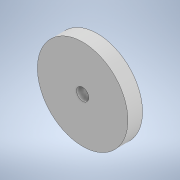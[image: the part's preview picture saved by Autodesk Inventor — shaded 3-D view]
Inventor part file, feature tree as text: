
AUTODESK INVENTOR PART (.ipt)
format: ipt  version: 2021 (Build 250183000, 183)  size: 98,816 bytes
history: native  units: mm
features: extrude x2, sketch x2
ambient origin geometry x8: Origin, YZ Plane, XZ Plane, XY Plane, X Axis, Y Axis, Z Axis, Center Point
bodies: Solid1 (feature_tree)
feature tree (4):
  extrude  "Extrusion1"  Depth=6.0mm TaperAngle=0.0deg
  extrude  "Extrusion2"  Depth=6.0mm TaperAngle=0.0deg
  sketch  "Sketch1"  dims[d0=37.0mm d1=6.0mm d2=0.0mm]
  sketch  "Sketch2"  dims[d3=5.0mm d4=6.0mm d5=0.0mm]
